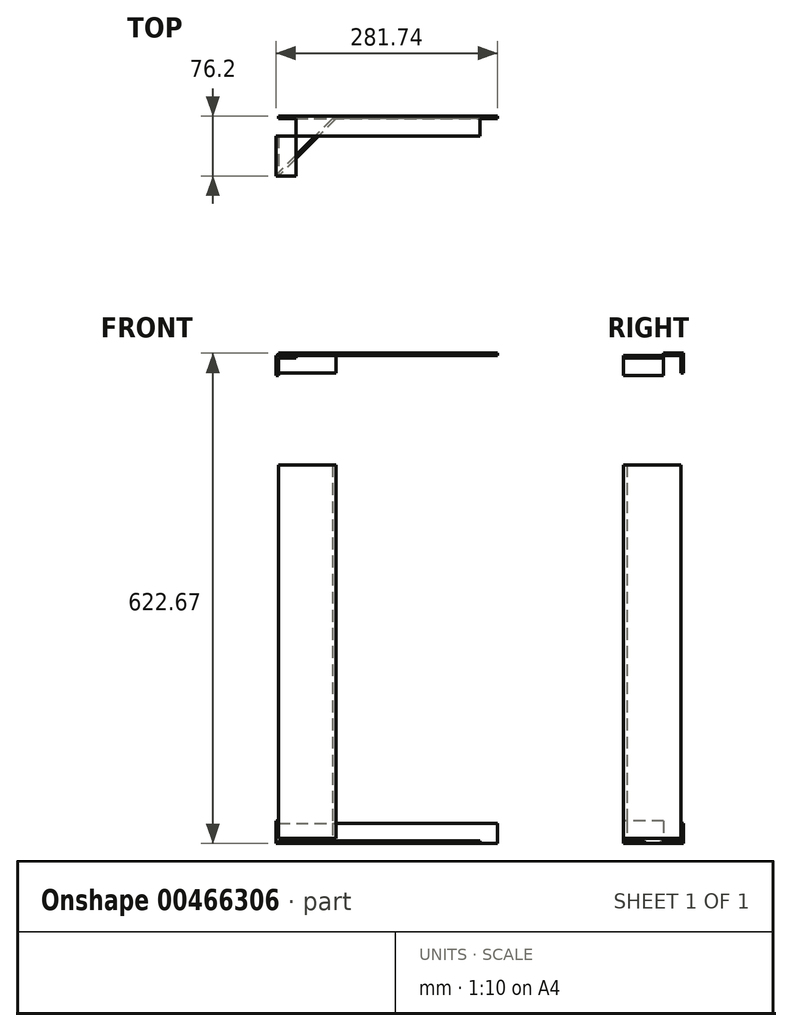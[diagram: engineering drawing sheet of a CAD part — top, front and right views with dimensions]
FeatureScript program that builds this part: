
annotation { "Feature Type Name" : "Feature", "Feature Type Description" : "" }
export const myFeature = defineFeature(function(context is Context, id is Id, definition is map)
    precondition{}
    {
        {
            var Q0;
            Q0=qCreatedBy(makeId("Top.planeOp"),FACE);
            var sketch = newSketch(context, id + "F0", { "sketchPlane" : qUnion([Q0])});
            skLineSegment(sketch, "E0.bottom", {"start": v(-38.1, 76.2) * mm, "end": v(-34.93, 76.2) * mm});
            skLineSegment(sketch, "E0.top", {"start": v(-38.1, 0) * mm, "end": v(-34.93, 0) * mm});
            skLineSegment(sketch, "E0.left", {"start": v(-38.1, 76.2) * mm, "end": v(-38.1, 0) * mm});
            skLineSegment(sketch, "E0.right", {"start": v(-34.93, 76.2) * mm, "end": v(-34.93, 0) * mm});
            skLineSegment(sketch, "E1.bottom", {"start": v(-38.1, 76.2) * mm, "end": v(38.1, 76.2) * mm});
            skLineSegment(sketch, "E1.top", {"start": v(-38.1, 73.03) * mm, "end": v(38.1, 73.03) * mm});
            skLineSegment(sketch, "E1.left", {"start": v(-38.1, 76.2) * mm, "end": v(-38.1, 73.03) * mm});
            skLineSegment(sketch, "E1.right", {"start": v(38.1, 76.2) * mm, "end": v(38.1, 73.03) * mm});
            skLineSegment(sketch, "E2", {"start": v(38.1, 73.03) * mm, "end": v(-34.93, 0) * mm});
            skLineSegment(sketch, "E3", {"start": v(33.6, 73.03) * mm, "end": v(-34.93, 4.5) * mm});
            skLineSegment(sketch, "E4.bottom", {"start": v(-38.1, 50.8) * mm, "end": v(38.1, 50.8) * mm});
            skLineSegment(sketch, "E4.left", {"start": v(-38.1, 50.8) * mm, "end": v(-38.1, 73.03) * mm});
            skLineSegment(sketch, "E4.right", {"start": v(38.1, 50.8) * mm, "end": v(38.1, 73.03) * mm});
            skLineSegment(sketch, "E5.bottom", {"start": v(-38.1, 0) * mm, "end": v(-12.7, 0) * mm});
            skLineSegment(sketch, "E5.top", {"start": v(-38.1, 73.03) * mm, "end": v(-12.7, 73.03) * mm});
            skLineSegment(sketch, "E5.left", {"start": v(-38.1, 0) * mm, "end": v(-38.1, 73.03) * mm});
            skLineSegment(sketch, "E5.right", {"start": v(-12.7, 0) * mm, "end": v(-12.7, 73.03) * mm});
            skLineSegment(sketch, "E6", {"start": v(-38.1, 47.62) * mm, "end": v(-34.93, 47.62) * mm});
            skSolve(sketch);
        }
        {
            var Q0;
            {var subQ0=sQuery(id+"F0.wireOp",EDGE,"E4.right");Q0=makeQuery(id+"F0.imprint","IMPRINT",FACE,{"disambiguationData":[TD([[makeQuery(id+"F0.imprint","IMPRINT",EDGE,{"derivedFrom":subQ0}),1.0]])]});}
            var Q1;
            {var subQ0=sQuery(id+"F0.wireOp",EDGE,"E1.top");var subQ5=sQuery(id+"F0.wireOp",EDGE,"E3");var subQ6=makeQuery(id+"F0.imprint","INTERSECT",VERTEX,{"derivedFrom":[subQ5,subQ0]});Q1=makeQuery(id+"F0.imprint","IMPRINT",FACE,{"disambiguationData":[TD([[makeQuery(id+"F0.imprint","IMPRINT",EDGE,{"disambiguationData":[TD([[subQ6,-1.0]])],"derivedFrom":subQ5}),1.0]])]});}
            var Q2;
            {var subQ0=sQuery(id+"F0.wireOp",EDGE,"E1.top");var subQ1=sQuery(id+"F0.wireOp",EDGE,"E3");var subQ2=makeQuery(id+"F0.imprint","INTERSECT",VERTEX,{"derivedFrom":[subQ1,subQ0]});Q2=makeQuery(id+"F0.imprint","IMPRINT",FACE,{"disambiguationData":[TD([[makeQuery(id+"F0.imprint","IMPRINT",EDGE,{"disambiguationData":[TD([[subQ2,-1.0]])],"derivedFrom":subQ1}),-1.0]])]});}
            var Q3;
            {var subQ0=sQuery(id+"F0.wireOp",EDGE,"E5.top");var subQ1=sQuery(id+"F0.wireOp",EDGE,"E0.right");var subQ2=makeQuery(id+"F0.imprint","INTERSECT",VERTEX,{"derivedFrom":[subQ1,subQ0]});Q3=makeQuery(id+"F0.imprint","IMPRINT",FACE,{"disambiguationData":[TD([[makeQuery(id+"F0.imprint","IMPRINT",EDGE,{"disambiguationData":[TD([[subQ2,-1.0]])],"derivedFrom":subQ1}),1.0]])]});}
            var Q4;
            {var subQ0=sQuery(id+"F0.wireOp",EDGE,"E5.top");var subQ1=sQuery(id+"F0.wireOp",EDGE,"E0.right");var subQ2=makeQuery(id+"F0.imprint","INTERSECT",VERTEX,{"derivedFrom":[subQ1,subQ0]});Q4=makeQuery(id+"F0.imprint","IMPRINT",FACE,{"disambiguationData":[TD([[makeQuery(id+"F0.imprint","IMPRINT",EDGE,{"disambiguationData":[TD([[subQ2,-1.0]])],"derivedFrom":subQ1}),-1.0]])]});}
            var Q5;
            {var subQ4=sQuery(id+"F0.wireOp",EDGE,"E1.right");Q5=makeQuery(id+"F0.imprint","IMPRINT",FACE,{"disambiguationData":[TD([[makeQuery(id+"F0.imprint","IMPRINT",EDGE,{"derivedFrom":subQ4}),-1.0]])]});}
            var Q6;
            {var subQ5=sQuery(id+"F0.wireOp",EDGE,"E1.left");Q6=makeQuery(id+"F0.imprint","IMPRINT",FACE,{"disambiguationData":[TD([[makeQuery(id+"F0.imprint","IMPRINT",EDGE,{"derivedFrom":subQ5}),1.0]])]});}
            extrude(context, id + "F1", {"entities" : qUnion([Q0, Q1, Q2, Q3, Q4, Q5, Q6]), "oppositeDirection" : true, "depth" : 3.17 * mm});
        }
        {
            var Q0;
            {var subQ0=sQuery(id+"F0.wireOp",EDGE,"E2");Q0=makeQuery(id+"F0.imprint","IMPRINT",FACE,{"disambiguationData":[TD([[makeQuery(id+"F0.imprint","IMPRINT",EDGE,{"derivedFrom":subQ0}),-1.0]])]});}
            extrude(context, id + "F2", {"entities" : qUnion([Q0]), "depth" : 477.4 * mm, "hasSecondDirection" : true, "secondDirectionOppositeDirection" : true, "secondDirectionDepth" : -3.17 * mm});
        }
        {
            var Q0;
            {var subQ4=sQuery(id+"F0.wireOp",EDGE,"E1.right");Q0=makeQuery(id+"F0.imprint","IMPRINT",FACE,{"disambiguationData":[TD([[makeQuery(id+"F0.imprint","IMPRINT",EDGE,{"derivedFrom":subQ4}),-1.0]])]});}
            var Q1;
            {var subQ5=sQuery(id+"F0.wireOp",EDGE,"E1.left");Q1=makeQuery(id+"F0.imprint","IMPRINT",FACE,{"disambiguationData":[TD([[makeQuery(id+"F0.imprint","IMPRINT",EDGE,{"derivedFrom":subQ5}),1.0]])]});}
            extrude(context, id + "F3", {"entities" : qUnion([Q0, Q1]), "operationType" : NewBodyOperationType.ADD, "depth" : 22.22 * mm});
        }
        {
            var Q0;
            Q0=makeQuery(id+"F1.opExtrude","CAP_FACE",FACE,{"disambiguationData":[OSD([sQuery(id+"F0.wireOp",EDGE,"E1.bottom"),sQuery(id+"F0.wireOp",EDGE,"E1.left"),sQuery(id+"F0.wireOp",EDGE,"E1.right"),sQuery(id+"F0.wireOp",EDGE,"E4.bottom"),sQuery(id+"F0.wireOp",EDGE,"E4.right"),sQuery(id+"F0.wireOp",EDGE,"E5.left")])],"isStart":false});
            extrude(context, id + "F4", {"entities" : qUnion([Q0]), "oppositeDirection" : true, "depth" : 622.68 * mm, "hasSecondDirection" : true, "secondDirectionOppositeDirection" : false, "secondDirectionDepth" : -619.5 * mm});
        }
        {
            var Q0;
            Q0=makeQuery(id+"F3.opExtrude","CAP_FACE",FACE,{"disambiguationData":[OSD([sQuery(id+"F0.wireOp",EDGE,"E1.bottom"),sQuery(id+"F0.wireOp",EDGE,"E1.left"),sQuery(id+"F0.wireOp",EDGE,"E1.right"),sQuery(id+"F0.wireOp",EDGE,"E1.top"),sQuery(id+"F0.wireOp",EDGE,"E5.top")])],"isStart":false});
            extrude(context, id + "F5", {"entities" : qUnion([Q0]), "operationType" : NewBodyOperationType.ADD, "depth" : 594.1 * mm, "hasSecondDirection" : true, "secondDirectionOppositeDirection" : false, "secondDirectionDepth" : 571.88 * mm});
        }
        {
            var Q0;
            {var subQ0=sQuery(id+"F0.wireOp",EDGE,"E5.bottom");var subQ3=sQuery(id+"F0.wireOp",EDGE,"E5.right");var subQ5=makeQuery(id+"F0.imprint","INTERSECT",VERTEX,{"derivedFrom":[subQ0,subQ3]});Q0=makeQuery(id+"F0.imprint","IMPRINT",FACE,{"disambiguationData":[TD([[makeQuery(id+"F0.imprint","IMPRINT",EDGE,{"disambiguationData":[TD([[subQ5,-1.0]])],"derivedFrom":subQ3}),1.0]])]});}
            var Q1;
            {var subQ1=sQuery(id+"F0.wireOp",EDGE,"E0.right");var subQ3=sQuery(id+"F0.wireOp",EDGE,"E3");var subQ4=makeQuery(id+"F0.imprint","INTERSECT",VERTEX,{"derivedFrom":[subQ1,subQ3]});Q1=makeQuery(id+"F0.imprint","IMPRINT",FACE,{"disambiguationData":[TD([[makeQuery(id+"F0.imprint","IMPRINT",EDGE,{"disambiguationData":[TD([[subQ4,1.0]])],"derivedFrom":subQ3}),1.0]])]});}
            var Q2;
            {var subQ1=sQuery(id+"F0.wireOp",EDGE,"E0.right");var subQ8=makeQuery(id+"F0.imprint","INTERSECT",VERTEX,{"derivedFrom":[subQ1,sQuery(id+"F0.wireOp",EDGE,"E6")]});Q2=makeQuery(id+"F0.imprint","IMPRINT",FACE,{"disambiguationData":[TD([[makeQuery(id+"F0.imprint","IMPRINT",EDGE,{"disambiguationData":[TD([[subQ8,1.0]])],"derivedFrom":subQ1}),1.0]])]});}
            var Q3;
            {var subQ0=sQuery(id+"F0.wireOp",EDGE,"E5.top");var subQ1=sQuery(id+"F0.wireOp",EDGE,"E0.right");var subQ2=makeQuery(id+"F0.imprint","INTERSECT",VERTEX,{"derivedFrom":[subQ1,subQ0]});Q3=makeQuery(id+"F0.imprint","IMPRINT",FACE,{"disambiguationData":[TD([[makeQuery(id+"F0.imprint","IMPRINT",EDGE,{"disambiguationData":[TD([[subQ2,-1.0]])],"derivedFrom":subQ1}),1.0]])]});}
            extrude(context, id + "F6", {"entities" : qUnion([Q0, Q1, Q2, Q3]), "depth" : 3.17 * mm});
        }
        {
            var Q0;
            {var subQ3=sQuery(id+"F0.wireOp",EDGE,"E6");Q0=makeQuery(id+"F0.imprint","IMPRINT",FACE,{"disambiguationData":[TD([[makeQuery(id+"F0.imprint","IMPRINT",EDGE,{"derivedFrom":subQ3}),-1.0]])]});}
            var Q1;
            {var subQ0=sQuery(id+"F0.wireOp",EDGE,"E5.top");var subQ1=sQuery(id+"F0.wireOp",EDGE,"E0.right");var subQ2=makeQuery(id+"F0.imprint","INTERSECT",VERTEX,{"derivedFrom":[subQ1,subQ0]});Q1=makeQuery(id+"F0.imprint","IMPRINT",FACE,{"disambiguationData":[TD([[makeQuery(id+"F0.imprint","IMPRINT",EDGE,{"disambiguationData":[TD([[subQ2,-1.0]])],"derivedFrom":subQ1}),-1.0]])]});}
            var Q2;
            {var subQ0=sQuery(id+"F0.wireOp",EDGE,"E6");Q2=makeQuery(id+"F0.imprint","IMPRINT",FACE,{"disambiguationData":[TD([[makeQuery(id+"F0.imprint","IMPRINT",EDGE,{"derivedFrom":subQ0}),1.0]])]});}
            extrude(context, id + "F7", {"entities" : qUnion([Q0, Q1, Q2]), "operationType" : NewBodyOperationType.ADD, "depth" : 25.4 * mm});
        }
        {
            var Q0;
            Q0=makeQuery(id+"F7.opExtrude","CAP_FACE",FACE,{"disambiguationData":[OSD([sQuery(id+"F0.wireOp",EDGE,"E0.right"),sQuery(id+"F0.wireOp",EDGE,"E5.bottom"),sQuery(id+"F0.wireOp",EDGE,"E5.top"),sQuery(id+"F0.wireOp",EDGE,"E5.left")])],"isStart":false});
            extrude(context, id + "F8", {"entities" : qUnion([Q0]), "depth" : 590.93 * mm, "hasSecondDirection" : true, "secondDirectionOppositeDirection" : true, "secondDirectionDepth" : -565.53 * mm});
        }
        {
            var Q0;
            Q0=makeQuery(id+"F6.opExtrude","CAP_FACE",FACE,{"disambiguationData":[OSD([sQuery(id+"F0.wireOp",EDGE,"E0.right"),sQuery(id+"F0.wireOp",EDGE,"E5.bottom"),sQuery(id+"F0.wireOp",EDGE,"E5.top"),sQuery(id+"F0.wireOp",EDGE,"E5.right")])],"isStart":false});
            extrude(context, id + "F9", {"entities" : qUnion([Q0]), "operationType" : NewBodyOperationType.ADD, "depth" : 613.15 * mm, "hasSecondDirection" : true, "secondDirectionOppositeDirection" : false, "secondDirectionDepth" : 609.98 * mm});
        }
        {
            var Q0;
            {var subQ0=sQuery(id+"F0.wireOp",EDGE,"E1.right");Q0=makeQuery(id+"F3.boolean.opBoolean","MERGE",FACE,{"derivedFrom":[makeQuery(id+"F1.opExtrude","SWEPT_FACE",FACE,{"disambiguationData":[OSD([subQ0,sQuery(id+"F0.wireOp",EDGE,"E4.right")])]}),makeQuery(id+"F3.opExtrude","SWEPT_FACE",FACE,{"disambiguationData":[OSD([subQ0])]})]});}
            var sketch = newSketch(context, id + "F10", { "sketchPlane" : qUnion([Q0])});
            skLineSegment(sketch, "E7", {"start": v(73.03, 0) * mm, "end": v(76.2, 0) * mm});
            skLineSegment(sketch, "E8", {"start": v(76.2, 0) * mm, "end": v(76.2, -3.18) * mm});
            skLineSegment(sketch, "E9", {"start": v(76.2, -3.18) * mm, "end": v(76.2, 22.23) * mm});
            skLineSegment(sketch, "E10", {"start": v(76.2, 22.23) * mm, "end": v(73.03, 22.23) * mm});
            skLineSegment(sketch, "E11", {"start": v(73.03, 22.23) * mm, "end": v(73.03, 0) * mm});
            skLineSegment(sketch, "E12", {"start": v(50.8, 0) * mm, "end": v(73.03, 0) * mm});
            skLineSegment(sketch, "E13", {"start": v(50.8, 0) * mm, "end": v(50.8, -3.18) * mm});
            skLineSegment(sketch, "E14", {"start": v(50.8, -3.18) * mm, "end": v(76.2, -3.18) * mm});
            skLineSegment(sketch, "E15.bottom", {"start": v(50.8, 616.33) * mm, "end": v(76.2, 616.33) * mm});
            skLineSegment(sketch, "E15.top", {"start": v(50.8, 619.5) * mm, "end": v(76.2, 619.5) * mm});
            skLineSegment(sketch, "E15.left", {"start": v(50.8, 616.33) * mm, "end": v(50.8, 619.5) * mm});
            skLineSegment(sketch, "E15.right", {"start": v(76.2, 616.33) * mm, "end": v(76.2, 619.5) * mm});
            skLineSegment(sketch, "E16.bottom", {"start": v(76.2, 616.33) * mm, "end": v(73.03, 616.33) * mm});
            skLineSegment(sketch, "E16.top", {"start": v(76.2, 594.1) * mm, "end": v(73.03, 594.1) * mm});
            skLineSegment(sketch, "E16.left", {"start": v(76.2, 616.33) * mm, "end": v(76.2, 594.1) * mm});
            skLineSegment(sketch, "E16.right", {"start": v(73.03, 616.33) * mm, "end": v(73.03, 594.1) * mm});
            skLineSegment(sketch, "E17", {"start": v(73.03, 616.33) * mm, "end": v(73.03, 619.5) * mm});
            skLineSegment(sketch, "E18", {"start": v(73.03, 0) * mm, "end": v(73.03, -3.18) * mm});
            skSolve(sketch);
        }
        {
            var Q0;
            {var subQ2=sQuery(id+"F10.wireOp",EDGE,"E7");Q0=makeQuery(id+"F10.imprint","IMPRINT",FACE,{"disambiguationData":[TD([[makeQuery(id+"F10.imprint","IMPRINT",EDGE,{"derivedFrom":subQ2}),-1.0]])]});}
            var Q1;
            {var subQ0=sQuery(id+"F10.wireOp",EDGE,"E7");Q1=makeQuery(id+"F10.imprint","IMPRINT",FACE,{"disambiguationData":[TD([[makeQuery(id+"F10.imprint","IMPRINT",EDGE,{"derivedFrom":subQ0}),1.0]])]});}
            extrude(context, id + "F11", {"entities" : qUnion([Q0, Q1]), "operationType" : NewBodyOperationType.ADD, "depth" : 205.54 * mm});
        }
        {
            var Q0;
            {var subQ0=sQuery(id+"F0.wireOp",EDGE,"E1.right");Q0=makeQuery(id+"F3.boolean.opBoolean","MERGE",FACE,{"derivedFrom":[makeQuery(id+"F1.opExtrude","SWEPT_FACE",FACE,{"disambiguationData":[OSD([subQ0,sQuery(id+"F0.wireOp",EDGE,"E4.right")])]}),makeQuery(id+"F3.opExtrude","SWEPT_FACE",FACE,{"disambiguationData":[OSD([subQ0])]})]});}
            extrude(context, id + "F12", {"entities" : qUnion([Q0]), "operationType" : NewBodyOperationType.ADD, "depth" : 183.32 * mm});
        }
        {
            var Q0;
            Q0=makeQuery(id+"F10.imprint","IMPRINT",FACE,{"disambiguationData":[TD([[makeQuery(id+"F10.imprint","IMPRINT",EDGE,{"derivedFrom":sQuery(id+"F10.wireOp",EDGE,"E16.bottom")}),1.0]])]});
            var Q1;
            {var subQ0=sQuery(id+"F10.wireOp",EDGE,"E15.right");Q1=makeQuery(id+"F10.imprint","IMPRINT",FACE,{"disambiguationData":[TD([[makeQuery(id+"F10.imprint","IMPRINT",EDGE,{"derivedFrom":subQ0}),1.0]])]});}
            extrude(context, id + "F13", {"entities" : qUnion([Q0, Q1]), "operationType" : NewBodyOperationType.ADD, "depth" : 205.54 * mm});
        }
        {
            var Q0;
            Q0=makeQuery(id+"F10.imprint","IMPRINT",FACE,{"disambiguationData":[TD([[makeQuery(id+"F10.imprint","IMPRINT",EDGE,{"derivedFrom":sQuery(id+"F10.wireOp",EDGE,"E15.bottom")}),1.0]])]});
            extrude(context, id + "F14", {"entities" : qUnion([Q0]), "operationType" : NewBodyOperationType.ADD, "depth" : 183.32 * mm});
        }
    });
